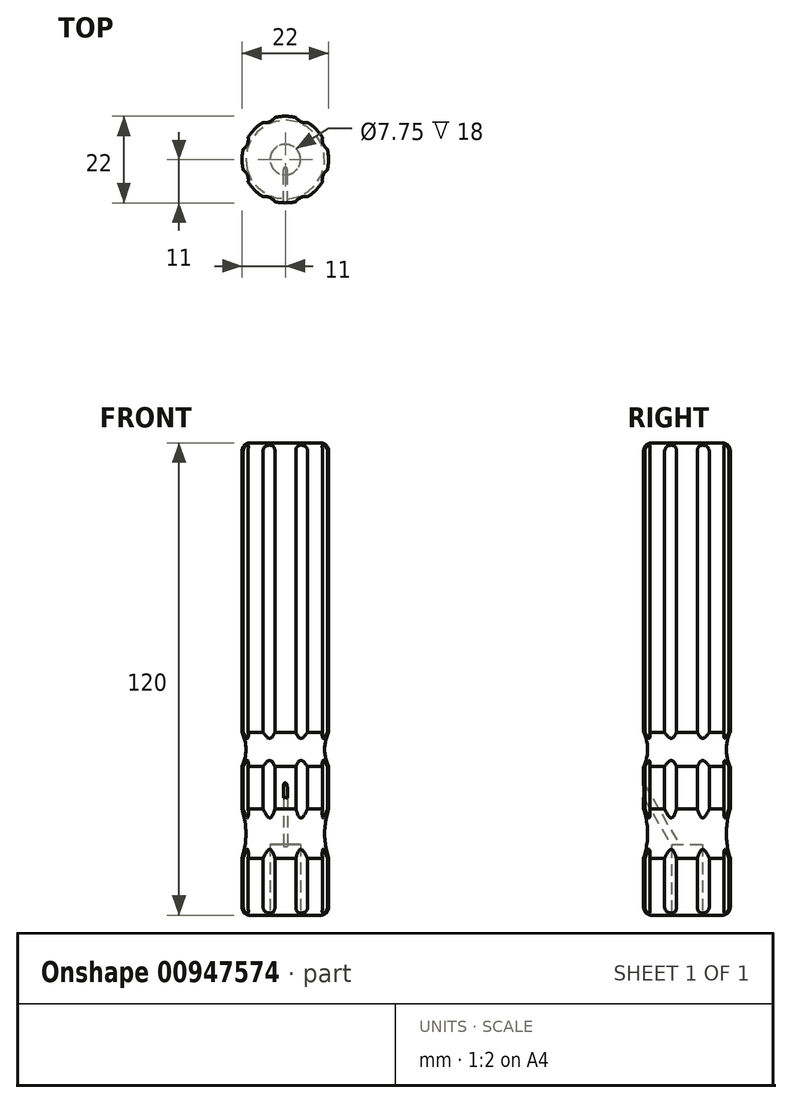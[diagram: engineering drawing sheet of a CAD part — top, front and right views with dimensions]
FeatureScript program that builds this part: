
annotation { "Feature Type Name" : "Feature", "Feature Type Description" : "" }
export const myFeature = defineFeature(function(context is Context, id is Id, definition is map)
    precondition{}
    {
        {
            var Q0;
            Q0=qCreatedBy(makeId("Front.planeOp"),FACE);
            var sketch = newSketch(context, id + "F0", { "sketchPlane" : qUnion([Q0])});
            skLineSegment(sketch, "E0", {"start": v(0, 0) * mm, "end": v(0, 120) * mm});
            skLineSegment(sketch, "E1", {"start": v(0, 120) * mm, "end": v(9, 120) * mm});
            skLineSegment(sketch, "E2", {"start": v(0, 0) * mm, "end": v(9, 0) * mm});
            skLineSegment(sketch, "E3", {"start": v(11, 118) * mm, "end": v(11, 46.5) * mm});
            skArc(sketch, "E4", {"start": v(11, 46.5) * mm, "mid": v(10, 42.14) * mm, "end": v(11, 37.78) * mm});
            skLineSegment(sketch, "E5", {"start": v(11, 37.78) * mm, "end": v(11, 26.99) * mm});
            skPoint(sketch, "E6.visualSharp", {"position": v(11, 0) * mm});
            skArc(sketch, "E6.filletArc", {"start": v(9, 0) * mm, "mid": v(10.41, 0.59) * mm, "end": v(11, 2) * mm});
            skPoint(sketch, "E7.visualSharp", {"position": v(11, 120) * mm});
            skArc(sketch, "E7.filletArc", {"start": v(11, 118) * mm, "mid": v(10.41, 119.41) * mm, "end": v(9, 120) * mm});
            skLineSegment(sketch, "E8.trimOffspring", {"start": v(11, 14.5) * mm, "end": v(11, 2) * mm});
            skArc(sketch, "E9", {"start": v(11, 26.99) * mm, "mid": v(10, 20.74) * mm, "end": v(11, 14.5) * mm});
            skSolve(sketch);
        }
        {
            var Q0;
            Q0 = qSketchRegion(id + "F0", true);
            var Q1;
            Q1=sQuery(id+"F0.wireOp",EDGE,"E0");
            revolve(context, id + "F1", {"surfaceOperationType" : NewSurfaceOperationType.NEW, "entities" : qUnion([Q0]), "axis" : qUnion([Q1]), "revolveType" : RevolveType.FULL});
        }
        {
            var Q0;
            Q0=qCreatedBy(makeId("Top.planeOp"),FACE);
            var sketch = newSketch(context, id + "F2", { "sketchPlane" : qUnion([Q0])});
            skLineSegment(sketch, "E10", {"start": v(0, 0) * mm, "end": v(54.68, -22.65) * mm, "construction": true});
            skLineSegment(sketch, "E11", {"start": v(0, 0) * mm, "end": v(-40.2, -16.65) * mm, "construction": true});
            skLineSegment(sketch, "E12", {"start": v(0, 0) * mm, "end": v(19.98, -48.22) * mm, "construction": true});
            skLineSegment(sketch, "E13", {"start": v(0, 0) * mm, "end": v(-16.24, -39.2) * mm, "construction": true});
            skCircle(sketch, "E14", {"center": v(12.38, -5.13) * mm, "radius": 3 * mm});
            skCircle(sketch, "E15", {"center": v(5.13, -12.38) * mm, "radius": 3 * mm});
            skCircle(sketch, "E16", {"center": v(-5.13, -12.38) * mm, "radius": 3 * mm});
            skCircle(sketch, "E17", {"center": v(-12.38, -5.13) * mm, "radius": 3 * mm});
            skCircle(sketch, "E18.MirrorC", {"center": v(-12.38, 5.13) * mm, "radius": 3 * mm});
            skCircle(sketch, "E19.MirrorC", {"center": v(-5.13, 12.38) * mm, "radius": 3 * mm});
            skCircle(sketch, "E20.MirrorC", {"center": v(5.13, 12.38) * mm, "radius": 3 * mm});
            skCircle(sketch, "E21.MirrorC", {"center": v(12.38, 5.13) * mm, "radius": 3 * mm});
            skSolve(sketch);
        }
        {
            var Q0;
            Q0 = qSketchRegion(id + "F2", true);
            extrude(context, id + "F3", {"entities" : qUnion([Q0]), "operationType" : NewBodyOperationType.REMOVE, "endBound" : BoundingType.THROUGH_ALL, "depth" : 25 * mm, "offsetDistance" : 25 * mm});
        }
        {
            var Q0;
            Q0=qCreatedBy(makeId("Top.planeOp"),FACE);
            var sketch = newSketch(context, id + "F4", { "sketchPlane" : qUnion([Q0])});
            skCircle(sketch, "E22", {"center": v(0, 0) * mm, "radius": 3.88 * mm});
            skSolve(sketch);
        }
        {
            var Q0;
            Q0 = qSketchRegion(id + "F4", true);
            extrude(context, id + "F5", {"entities" : qUnion([Q0]), "operationType" : NewBodyOperationType.REMOVE, "depth" : 18 * mm, "offsetDistance" : 25 * mm});
        }
        {
            var Q0;
            Q0=makeQuery(id+"F5.boolean.opBoolean","COPY",FACE,{"derivedFrom":makeQuery(id+"F5.opExtrude","CAP_FACE",FACE,{"disambiguationData":[OSD([sQuery(id+"F4.wireOp",EDGE,"E22")])],"isStart":false})});
            var sketch = newSketch(context, id + "F6", { "sketchPlane" : qUnion([Q0])});
            skLineSegment(sketch, "E23", {"start": v(0, -3.88) * mm, "end": v(0, 2.52) * mm, "construction": true});
            skLineSegment(sketch, "E24", {"start": v(-11.58, 2.52) * mm, "end": v(15.94, 2.52) * mm, "construction": true});
            skSolve(sketch);
        }
        {
            var Q0;
            Q0=makeQuery(id+"F6.imprint","IMPRINT",FACE,{"disambiguationData":[TD([[makeQuery(id+"F6.imprint","IMPRINT",EDGE,{"derivedFrom":makeQuery(id+"F5.boolean.opBoolean","COPY",EDGE,{"derivedFrom":makeQuery(id+"F5.opExtrude","CAP_EDGE",EDGE,{"disambiguationData":[OSD([sQuery(id+"F4.wireOp",EDGE,"E22")])],"isStart":false})})}),-1.0]])]});
            var Q1;
            Q1=sQuery(id+"F6.wireOp",EDGE,"E24");
            cPlane(context, id + "F7", {"entities" : qUnion([Q0, Q1]), "cplaneType" : CPlaneType.LINE_ANGLE, "offset" : 25 * mm, "angle" : 30 * degree, "width" : 150 * mm, "height" : 150 * mm});
        }
        {
            var Q0;
            Q0=qCreatedBy(id+"F7.planeOp",FACE);
            var sketch = newSketch(context, id + "F8", { "sketchPlane" : qUnion([Q0])});
            skArc(sketch, "E25", {"start": v(0.5, 6.81) * mm, "mid": v(0, 7.31) * mm, "end": v(-0.5, 6.81) * mm});
            skLineSegment(sketch, "E26", {"start": v(0.5, 6.81) * mm, "end": v(0.5, 5.41) * mm});
            skLineSegment(sketch, "E27", {"start": v(-0.5, 6.81) * mm, "end": v(-0.5, 5.41) * mm});
            skLineSegment(sketch, "E28", {"start": v(-0.5, 5.41) * mm, "end": v(0.5, 5.41) * mm});
            skSolve(sketch);
        }
        {
            var Q0;
            Q0 = qSketchRegion(id + "F8", true);
            var Q1;
            Q1=makeQuery(id+"F5.boolean.opBoolean","COPY",FACE,{"derivedFrom":makeQuery(id+"F5.opExtrude","SWEPT_FACE",FACE,{"disambiguationData":[OSD([sQuery(id+"F4.wireOp",EDGE,"E22")])]})});
            extrude(context, id + "F9", {"entities" : qUnion([Q0]), "operationType" : NewBodyOperationType.REMOVE, "endBound" : BoundingType.THROUGH_ALL, "depth" : 25 * mm, "offsetDistance" : 25 * mm, "hasSecondDirection" : true, "secondDirectionBound" : SecondDirectionBoundingType.UP_TO_SURFACE, "secondDirectionOppositeDirection" : true, "secondDirectionDepth" : 25 * mm, "secondDirectionBoundEntityFace" : qUnion([Q1])});
        }
    });
